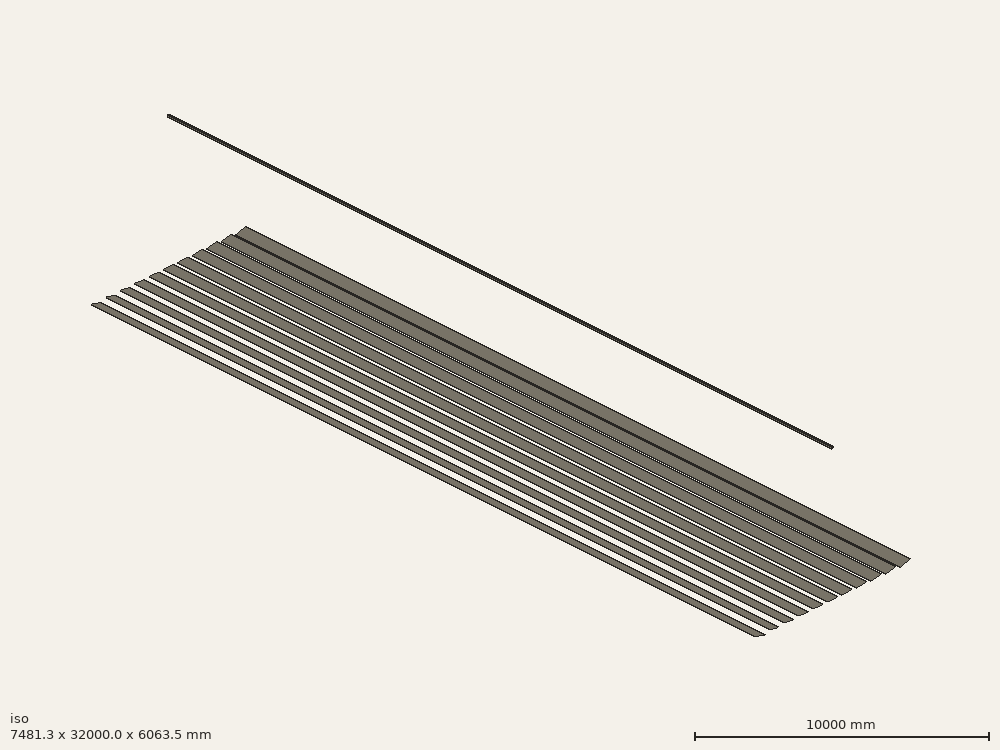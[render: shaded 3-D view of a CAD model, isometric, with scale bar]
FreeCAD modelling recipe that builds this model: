
FCSTD DOCUMENT  (FreeCAD 0.18R4 (GitTag))
Label: LFR
License: All rights reserved
LicenseURL: http://en.wikipedia.org/wiki/All_rights_reserved
objects: Part::Line×22, Part::Feature×15, Part::Extrusion×13, Part::Plane×1
note: 51 computed .brp shape members not serialized (recipe doc carries the construction recipe); baked Part::Feature solids carry a one-line shape summary decoded from their .brp

FEATURE [Part::Feature] Parabola
  Placement = pos=(-3500,0,0) rot=(-0.679153,-0.519014,-0.519014;1.9484rad)
  shape: bbox 482.5 x 2e-07 x 131.3 mm, 0 faces, 0 solids (baked)
FEATURE [Part::Extrusion] Extruded_parabola__5  label="Extruded_parabola__5(Mir1,Axis__5,Normal__5,Target)"
  Base = -> Parabola
  Dir = (0,32000,0)
  DirMode = 0
  FaceMakerClass = Part::FaceMakerExtrusion
  LengthFwd = 0
  LengthRev = 0
  Solid = false
  Symmetric = false
FEATURE [Part::Line] Normal__5
  AttacherType = Attacher::AttachEngine3D
  X1 = -3500
  X2 = -3499.74
  Y1 = 0
  Y2 = 0
  Z1 = 0
  Z2 = 0.964901
FEATURE [Part::Line] Axis__5
  AttacherType = Attacher::AttachEngine3D
  X1 = -3500
  X2 = -3500
  Y1 = 0
  Y2 = 32000
  Z1 = 0
  Z2 = 0
FEATURE [Part::Feature] Parabola001
  Placement = pos=(-2800,0,0) rot=(-0.661691,-0.530172,-0.530172;1.97249rad)
  shape: bbox 488 x 2e-07 x 109 mm, 0 faces, 0 solids (baked)
FEATURE [Part::Extrusion] Extruded_parabola__4  label="Extruded_parabola__4(Mir1,Axis__4,Normal__4,Target)"
  Base = -> Parabola001
  Dir = (0,32000,0)
  DirMode = 0
  FaceMakerClass = Part::FaceMakerExtrusion
  LengthFwd = 0
  LengthRev = 0
  Solid = false
  Symmetric = false
FEATURE [Part::Line] Normal__4
  AttacherType = Attacher::AttachEngine3D
  X1 = -2800
  X2 = -2799.78
  Y1 = 0
  Y2 = 0
  Z1 = 0
  Z2 = 0.97594
FEATURE [Part::Line] Axis__4
  AttacherType = Attacher::AttachEngine3D
  X1 = -2800
  X2 = -2800
  Y1 = 0
  Y2 = 32000
  Z1 = 0
  Z2 = 0
FEATURE [Part::Feature] Parabola002
  Placement = pos=(-2100,0,0) rot=(-0.642495,-0.541849,-0.541849;1.99943rad)
  shape: bbox 492.8 x 2e-07 x 84.37 mm, 0 faces, 0 solids (baked)
FEATURE [Part::Extrusion] Extruded_parabola__3  label="Extruded_parabola__3(Mir1,Axis__3,Normal__3,Target)"
  Base = -> Parabola002
  Dir = (0,32000,0)
  DirMode = 0
  FaceMakerClass = Part::FaceMakerExtrusion
  LengthFwd = 0
  LengthRev = 0
  Solid = false
  Symmetric = false
FEATURE [Part::Line] Normal__3
  AttacherType = Attacher::AttachEngine3D
  X1 = -2100
  X2 = -2099.83
  Y1 = 0
  Y2 = 0
  Z1 = 0
  Z2 = 0.98566
FEATURE [Part::Line] Axis__3
  AttacherType = Attacher::AttachEngine3D
  X1 = -2100
  X2 = -2100
  Y1 = 0
  Y2 = 32000
  Z1 = 0
  Z2 = 0
FEATURE [Part::Feature] Parabola003
  Placement = pos=(-1400,0,0) rot=(-0.621763,-0.55381,-0.55381;2.02906rad)
  shape: bbox 496.7 x 2e-07 x 57.61 mm, 0 faces, 0 solids (baked)
FEATURE [Part::Extrusion] Extruded_parabola__2  label="Extruded_parabola__2(Mir1,Axis__2,Normal__2,Target)"
  Base = -> Parabola003
  Dir = (0,32000,0)
  DirMode = 0
  FaceMakerClass = Part::FaceMakerExtrusion
  LengthFwd = 0
  LengthRev = 0
  Solid = false
  Symmetric = false
FEATURE [Part::Line] Normal__2
  AttacherType = Attacher::AttachEngine3D
  X1 = -1400
  X2 = -1399.88
  Y1 = 0
  Y2 = 0
  Z1 = 0
  Z2 = 0.99334
FEATURE [Part::Line] Axis__2
  AttacherType = Attacher::AttachEngine3D
  X1 = -1400
  X2 = -1400
  Y1 = 0
  Y2 = 32000
  Z1 = 0
  Z2 = 0
FEATURE [Part::Feature] Parabola004
  Placement = pos=(-700,0,0) rot=(-0.59987,-0.565754,-0.565754;2.06094rad)
  shape: bbox 499.1 x 2e-07 x 29.24 mm, 0 faces, 0 solids (baked)
FEATURE [Part::Extrusion] Extruded_parabola__1  label="Extruded_parabola__1(Mir1,Axis__1,Normal__1,Target)"
  Base = -> Parabola004
  Dir = (0,32000,0)
  DirMode = 0
  FaceMakerClass = Part::FaceMakerExtrusion
  LengthFwd = 0
  LengthRev = 0
  Solid = false
  Symmetric = false
FEATURE [Part::Line] Normal__1
  AttacherType = Attacher::AttachEngine3D
  X1 = -700
  X2 = -699.942
  Y1 = 0
  Y2 = 0
  Z1 = 0
  Z2 = 0.998288
FEATURE [Part::Line] Axis__1
  AttacherType = Attacher::AttachEngine3D
  X1 = -700
  X2 = -700
  Y1 = 0
  Y2 = 32000
  Z1 = 0
  Z2 = 0
FEATURE [Part::Feature] Parabola005
  Placement = pos=(0,0,0) rot=(0.57735,0.57735,0.57735;4.18879rad)
  shape: bbox 500 x 2e-07 x 2.624 mm, 0 faces, 0 solids (baked)
FEATURE [Part::Extrusion] Extruded_parabola_0  label="Extruded_parabola_0(Mir1,Axis_0,Normal_0,Target)"
  Base = -> Parabola005
  Dir = (0,32000,0)
  DirMode = 0
  FaceMakerClass = Part::FaceMakerExtrusion
  LengthFwd = 0
  LengthRev = 0
  Solid = false
  Symmetric = false
FEATURE [Part::Line] Normal_0
  AttacherType = Attacher::AttachEngine3D
  X1 = 0
  X2 = 0
  Y1 = 0
  Y2 = 0
  Z1 = 0
  Z2 = 1
FEATURE [Part::Line] Axis_0
  AttacherType = Attacher::AttachEngine3D
  X1 = 0
  X2 = 0
  Y1 = 0
  Y2 = 32000
  Z1 = 0
  Z2 = 0
FEATURE [Part::Feature] Parabola006
  Placement = pos=(700,0,0) rot=(0.55483,0.588287,0.588287;4.15468rad)
  shape: bbox 499.1 x 2e-07 x 29.24 mm, 0 faces, 0 solids (baked)
FEATURE [Part::Extrusion] Extruded_parabola_1  label="Extruded_parabola_1(Mir1,Axis_1,Normal_1,Target)"
  Base = -> Parabola006
  Dir = (0,32000,0)
  DirMode = 0
  FaceMakerClass = Part::FaceMakerExtrusion
  LengthFwd = 0
  LengthRev = 0
  Solid = false
  Symmetric = false
FEATURE [Part::Line] Normal_1
  AttacherType = Attacher::AttachEngine3D
  X1 = 700
  X2 = 699.942
  Y1 = 0
  Y2 = 0
  Z1 = 0
  Z2 = 0.998288
FEATURE [Part::Line] Axis_1
  AttacherType = Attacher::AttachEngine3D
  X1 = 700
  X2 = 700
  Y1 = 0
  Y2 = 32000
  Z1 = 0
  Z2 = 0
FEATURE [Part::Feature] Parabola007
  Placement = pos=(1400,0,0) rot=(0.532933,0.598324,0.598324;4.12088rad)
  shape: bbox 496.7 x 2e-07 x 57.61 mm, 0 faces, 0 solids (baked)
FEATURE [Part::Extrusion] Extruded_parabola_2  label="Extruded_parabola_2(Mir1,Axis_2,Normal_2,Target)"
  Base = -> Parabola007
  Dir = (0,32000,0)
  DirMode = 0
  FaceMakerClass = Part::FaceMakerExtrusion
  LengthFwd = 0
  LengthRev = 0
  Solid = false
  Symmetric = false
FEATURE [Part::Line] Normal_2
  AttacherType = Attacher::AttachEngine3D
  X1 = 1400
  X2 = 1399.88
  Y1 = 0
  Y2 = 0
  Z1 = 0
  Z2 = 0.99334
FEATURE [Part::Line] Axis_2
  AttacherType = Attacher::AttachEngine3D
  X1 = 1400
  X2 = 1400
  Y1 = 0
  Y2 = 32000
  Z1 = 0
  Z2 = 0
FEATURE [Part::Feature] Parabola008
  Placement = pos=(2100,0,0) rot=(0.512182,0.607318,0.607318;4.08828rad)
  shape: bbox 492.8 x 2e-07 x 84.37 mm, 0 faces, 0 solids (baked)
FEATURE [Part::Extrusion] Extruded_parabola_3  label="Extruded_parabola_3(Mir1,Axis_3,Normal_3,Target)"
  Base = -> Parabola008
  Dir = (0,32000,0)
  DirMode = 0
  FaceMakerClass = Part::FaceMakerExtrusion
  LengthFwd = 0
  LengthRev = 0
  Solid = false
  Symmetric = false
FEATURE [Part::Line] Normal_3
  AttacherType = Attacher::AttachEngine3D
  X1 = 2100
  X2 = 2099.83
  Y1 = 0
  Y2 = 0
  Z1 = 0
  Z2 = 0.98566
FEATURE [Part::Line] Axis_3
  AttacherType = Attacher::AttachEngine3D
  X1 = 2100
  X2 = 2100
  Y1 = 0
  Y2 = 32000
  Z1 = 0
  Z2 = 0
FEATURE [Part::Feature] Parabola009
  Placement = pos=(2800,0,0) rot=(0.492943,0.615227,0.615227;4.05756rad)
  shape: bbox 488 x 2e-07 x 109 mm, 0 faces, 0 solids (baked)
FEATURE [Part::Extrusion] Extruded_parabola_4  label="Extruded_parabola_4(Mir1,Axis_4,Normal_4,Target)"
  Base = -> Parabola009
  Dir = (0,32000,0)
  DirMode = 0
  FaceMakerClass = Part::FaceMakerExtrusion
  LengthFwd = 0
  LengthRev = 0
  Solid = false
  Symmetric = false
FEATURE [Part::Line] Normal_4
  AttacherType = Attacher::AttachEngine3D
  X1 = 2800
  X2 = 2799.78
  Y1 = 0
  Y2 = 0
  Z1 = 0
  Z2 = 0.97594
FEATURE [Part::Line] Axis_4
  AttacherType = Attacher::AttachEngine3D
  X1 = 2800
  X2 = 2800
  Y1 = 0
  Y2 = 32000
  Z1 = 0
  Z2 = 0
FEATURE [Part::Feature] Parabola010
  Placement = pos=(3500,0,0) rot=(0.475405,0.622089,0.622089;4.02915rad)
  shape: bbox 482.5 x 2e-07 x 131.3 mm, 0 faces, 0 solids (baked)
FEATURE [Part::Extrusion] Extruded_parabola_5  label="Extruded_parabola_5(Mir1,Axis_5,Normal_5,Target)"
  Base = -> Parabola010
  Dir = (0,32000,0)
  DirMode = 0
  FaceMakerClass = Part::FaceMakerExtrusion
  LengthFwd = 0
  LengthRev = 0
  Solid = false
  Symmetric = false
FEATURE [Part::Line] Normal_5
  AttacherType = Attacher::AttachEngine3D
  X1 = 3500
  X2 = 3499.74
  Y1 = 0
  Y2 = 0
  Z1 = 0
  Z2 = 0.964901
FEATURE [Part::Line] Axis_5
  AttacherType = Attacher::AttachEngine3D
  X1 = 3500
  X2 = 3500
  Y1 = 0
  Y2 = 32000
  Z1 = 0
  Z2 = 0
FEATURE [Part::Feature] Target
  shape: bbox 2e-07 x 2e-07 x 2e-07 mm, 0 faces, 0 solids (baked)
FEATURE [Part::Feature] Parabola1
  Placement = pos=(1.26013,0,6044.77) rot=(-0.817269,0.407475,0.407475;1.77123rad)
  shape: bbox 18.7 x 2e-07 x 61.81 mm, 0 faces, 0 solids (baked)
FEATURE [Part::Extrusion] Extruded_CPC_1  label="Extruded_CPC_1(Mir2)"
  Base = -> Parabola1
  Dir = (0,32000,0)
  DirMode = 0
  FaceMakerClass = Part::FaceMakerExtrusion
  LengthFwd = 0
  LengthRev = 0
  Solid = false
  Symmetric = false
FEATURE [Part::Feature] Parabola2
  Placement = pos=(-1.26013,0,6044.77) rot=(-0.332492,0.666877,0.666877;2.49961rad)
  shape: bbox 18.7 x 2e-07 x 61.81 mm, 0 faces, 0 solids (baked)
FEATURE [Part::Extrusion] Extruded_CPC_2  label="Extruded_CPC_2(Mir2)"
  Base = -> Parabola2
  Dir = (0,32000,0)
  DirMode = 0
  FaceMakerClass = Part::FaceMakerExtrusion
  LengthFwd = 0
  LengthRev = 0
  Solid = false
  Symmetric = false
FEATURE [Part::Plane] Receiver  label="Receiver(Abs)"
  AttacherType = Attacher::AttachEngine3D
  Length = 70
  Placement = pos=(-35,0,6000) rot=(0,0,1;0rad)
  Width = 32000
FEATURE [Part::Feature] Face005  label="Cover(Trans)"
  Placement = pos=(-53.6989,0,5934.19) rot=(0,0,1;0rad)
  shape: bbox 107.4 x 32000 x 2e-07 mm, 1 faces, 0 solids (baked)
